# Revit family: groove_l_1455_ab_led_26w_1704lm_cri80_3000k_340-2040_aac6
name_source: partatom
category: Leuchten
revit_build: Autodesk Revit 2016 (Build: 20190508_0715(x64)
units: mm (PartAtom-declared; Revit-internal decimal feet)

## family parameters
Basisbauteil = Fläche
Beim Laden mit Abzugskörper schneiden = Nein
Bemaßung runder Anschluss = Durchmesser verwenden
Gemeinsam genutzt = Nein
Lichtquelle = Nein
Raumberechnungspunkt = Nein
Teiletyp = Normal

## types (1)
- 340-2040- (5 x LED, 710 lm, 5.1 W, 3000K)
    Beschreibung = The surface luminaire GROOVE from the familiy GROOVE consists of aluminum-extruded profile. Charming SOFT-EDGE design ensure unparalleled styling. The ballast is integrated and allows for an operation with 220-240V (50/60Hz). GROOVE (# 340-2040) ist not dimmable (on/off). The luminaire with direct illumination and corresponds to protection class SK1 at IP20.
    CIE Flux Codes = 59 87 97 100 49
    Color Rendering = 1B/80…89
    Color Temperature = 3000K
    Height = 120 mm
    Hersteller = Prolicht
    Lamp Light Flux = 710 lm
    Lamp Power = 5.1 W
    Lamp count = 5
    Lampe = 5 x LED
    Length = 1455 mm
    Luminous efficacy = 67 lm/W
    ModVariant = Nein
    Modell = 340-2040
    Mounting Place = Ceiling
    Mounting Type = Surface mounted
    Number of Poles = 1
    OnlyDefault = Ja
    Power Factor = 1
    Product Name = GROOVE L=1455 AB LED 26W 1704lm CRI80 3000K
    Product group = Surface profile lights
    ProductGroupID = 334
    Protection Class = Protection class
    Protection Degree = Degree of protection
    RLX_Detail_Level = 1
    RlxData = <blob elided: 56741 chars, md5=886c7a30>
    Scheinlast = 26 VA
    Socket = socket
    Standby Power = 0 W
    System Light Flux = 1712 lm
    System Power = 26 W
    Typenbild = 340-2040.jpg
    URL = http://relux.com
    VarID = 340-2040-
    Voltage = 0 V
    Vorgabe-Ansicht = 1800 mm
    Weight = 0.00 kg
    Width = 80 mm  [stored 0.262467 ft]

note: [stored X ft] marks values corroborated as IEEE doubles in the binary element streams (Revit-internal decimal feet)

## geometry (parser evidence)
native form markers: Blend x4, Sweep x12
no freeform markers — native parametric forms only
